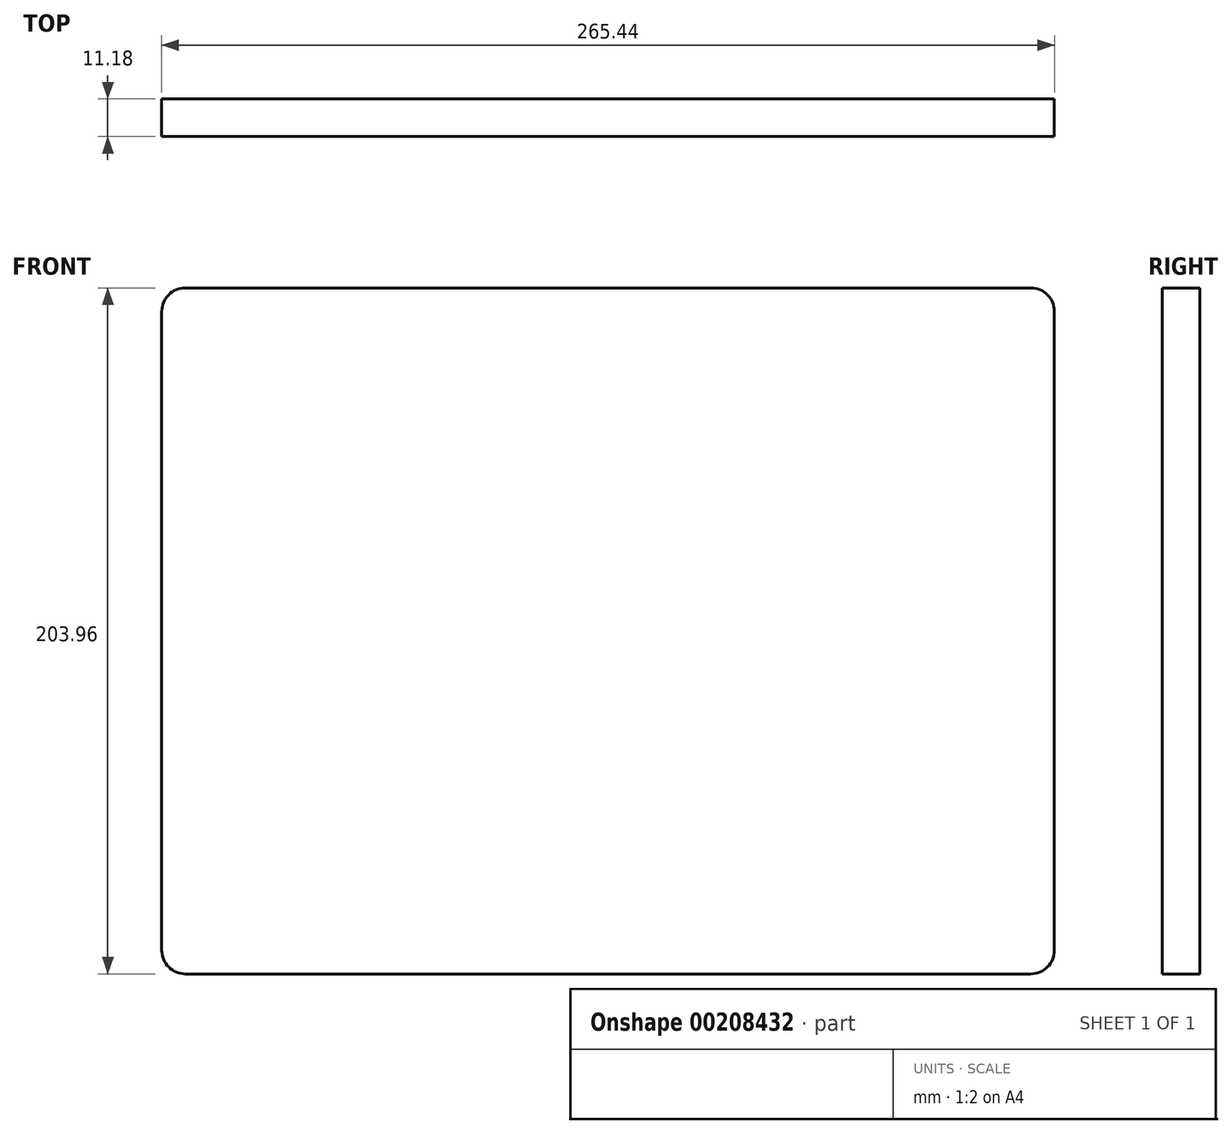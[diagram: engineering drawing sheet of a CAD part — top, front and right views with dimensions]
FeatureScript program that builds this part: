
annotation { "Feature Type Name" : "Feature", "Feature Type Description" : "" }
export const myFeature = defineFeature(function(context is Context, id is Id, definition is map)
    precondition{}
    {
        {
            var Q0;
            Q0=qCreatedBy(makeId("Front.planeOp"),FACE);
            var sketch = newSketch(context, id + "F0", { "sketchPlane" : qUnion([Q0])});
            skLineSegment(sketch, "E0.bottom", {"start": v(114.3, 92.71) * mm, "end": v(-114.3, 92.71) * mm});
            skLineSegment(sketch, "E0.top", {"start": v(114.3, -92.71) * mm, "end": v(-114.3, -92.71) * mm});
            skLineSegment(sketch, "E0.left", {"start": v(120.65, 86.36) * mm, "end": v(120.65, -86.36) * mm});
            skLineSegment(sketch, "E0.right", {"start": v(-120.65, 86.36) * mm, "end": v(-120.65, -86.36) * mm});
            skPoint(sketch, "E0.middle", {"position": v(0, 0) * mm});
            skPoint(sketch, "E1.visualSharp", {"position": v(-120.65, 92.71) * mm});
            skArc(sketch, "E1.filletArc", {"start": v(-114.3, 92.71) * mm, "mid": v(-118.8, 90.85) * mm, "end": v(-120.65, 86.36) * mm});
            skPoint(sketch, "E2.visualSharp", {"position": v(120.65, 92.71) * mm});
            skArc(sketch, "E2.filletArc", {"start": v(120.65, 86.36) * mm, "mid": v(118.8, 90.85) * mm, "end": v(114.3, 92.71) * mm});
            skPoint(sketch, "E3.visualSharp", {"position": v(120.65, -92.71) * mm});
            skArc(sketch, "E3.filletArc", {"start": v(114.3, -92.71) * mm, "mid": v(118.8, -90.85) * mm, "end": v(120.65, -86.36) * mm});
            skPoint(sketch, "E4.visualSharp", {"position": v(-120.65, -92.71) * mm});
            skArc(sketch, "E4.filletArc", {"start": v(-120.65, -86.36) * mm, "mid": v(-118.8, -90.85) * mm, "end": v(-114.3, -92.71) * mm});
            skSolve(sketch);
        }
        {
            var Q0;
            Q0=qSketchRegion(id+"F0",true);
            extrude(context, id + "F1", {"entities" : qUnion([Q0]), "depth" : 10.16 * mm});
        }
        {
            var Q0;
            Q0=makeQuery(id+"F1.opExtrude","SWEPT_BODY",BODY,{"disambiguationData":[OSD([sQuery(id+"F0.wireOp",EDGE,"E0.bottom"),sQuery(id+"F0.wireOp",EDGE,"E0.top"),sQuery(id+"F0.wireOp",EDGE,"E0.left"),sQuery(id+"F0.wireOp",EDGE,"E0.right"),sQuery(id+"F0.wireOp",EDGE,"E1.filletArc"),sQuery(id+"F0.wireOp",EDGE,"E2.filletArc"),sQuery(id+"F0.wireOp",EDGE,"E3.filletArc"),sQuery(id+"F0.wireOp",EDGE,"E4.filletArc")])]});
            var Q1;
            Q1=qCreatedBy(makeId("Origin.pointOp"),VERTEX);
            transform(context, id + "F2", {"entities" : qUnion([Q0]), "transformType" : TransformType.SCALE_UNIFORMLY, "scale" : 1.1, "scalePoint" : qUnion([Q1]), "makeCopy" : false});
        }
    });
